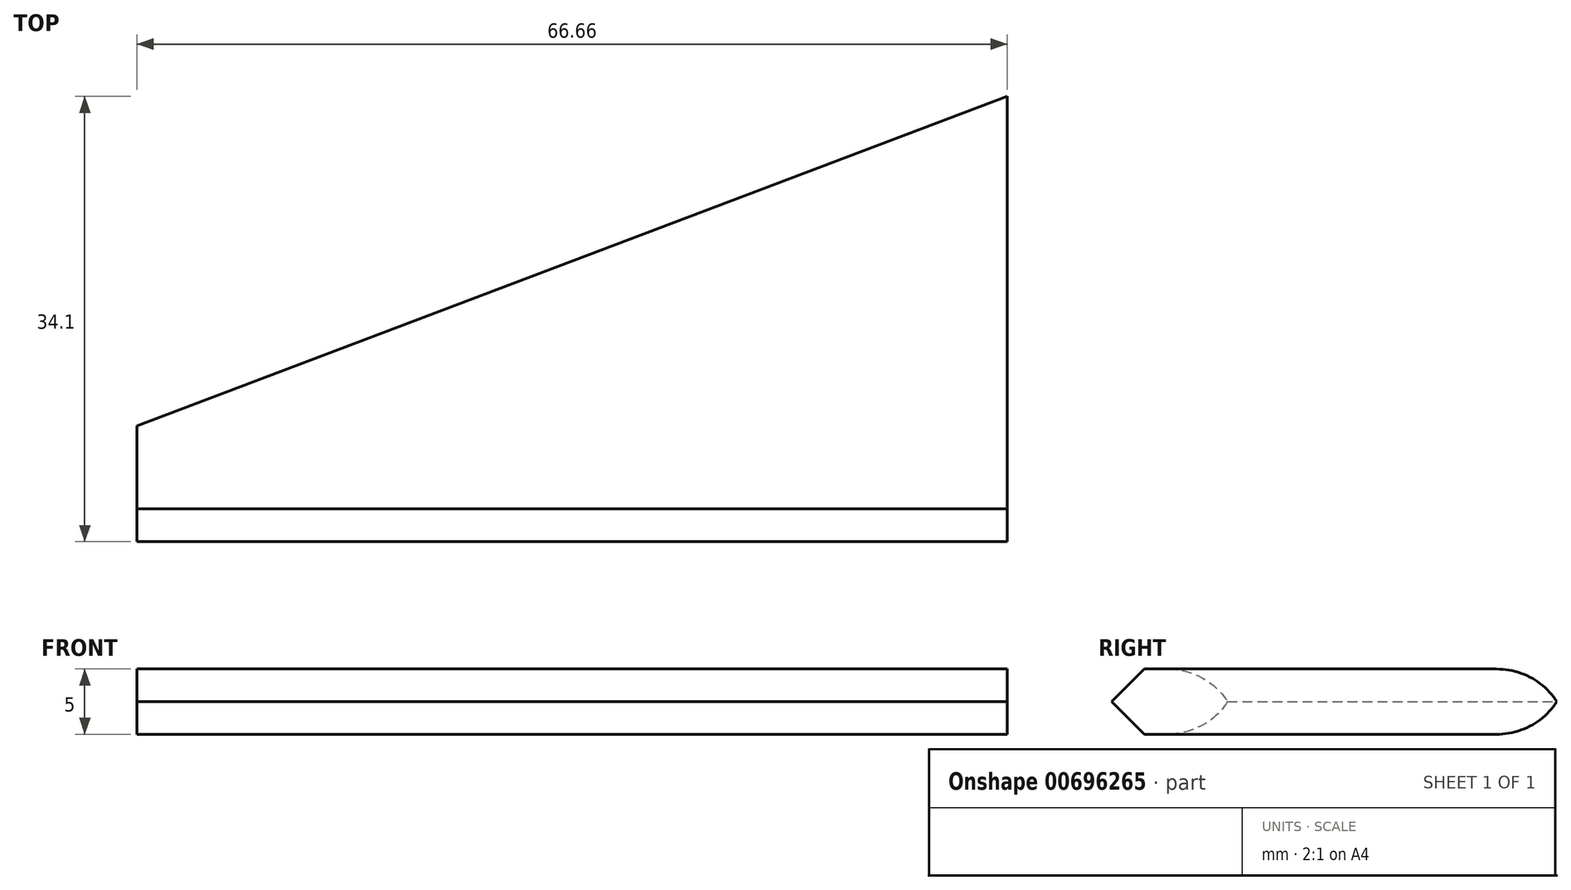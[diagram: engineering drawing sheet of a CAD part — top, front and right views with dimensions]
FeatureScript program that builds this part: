
annotation { "Feature Type Name" : "Feature", "Feature Type Description" : "" }
export const myFeature = defineFeature(function(context is Context, id is Id, definition is map)
    precondition{}
    {
        {
            var Q0;
            Q0=qCreatedBy(makeId("Top.planeOp"),FACE);
            var sketch = newSketch(context, id + "F0", { "sketchPlane" : qUnion([Q0])});
            skLineSegment(sketch, "E0.bottom", {"start": v(33.33, -6.05) * mm, "end": v(-33.33, -6.05) * mm});
            skLineSegment(sketch, "E0.top", {"start": v(33.33, 6.05) * mm, "end": v(-33.33, 6.05) * mm});
            skLineSegment(sketch, "E0.left", {"start": v(33.33, -6.05) * mm, "end": v(33.33, 6.05) * mm});
            skLineSegment(sketch, "E0.right", {"start": v(-33.33, -6.05) * mm, "end": v(-33.33, 6.05) * mm});
            skPoint(sketch, "E0.middle", {"position": v(0, 0) * mm});
            skLineSegment(sketch, "E1", {"start": v(-33.33, 6.05) * mm, "end": v(33.33, 31.27) * mm});
            skLineSegment(sketch, "E2", {"start": v(33.33, 31.27) * mm, "end": v(33.33, 6.05) * mm});
            skSolve(sketch);
        }
        {
            var Q0;
            Q0=makeQuery(id+"F0.imprint","IMPRINT",FACE,{"disambiguationData":[TD([[makeQuery(id+"F0.imprint","IMPRINT",EDGE,{"derivedFrom":sQuery(id+"F0.wireOp",EDGE,"E0.top")}),-1.0]])]});
            var Q1;
            Q1=makeQuery(id+"F0.imprint","IMPRINT",FACE,{"disambiguationData":[TD([[makeQuery(id+"F0.imprint","IMPRINT",EDGE,{"derivedFrom":sQuery(id+"F0.wireOp",EDGE,"E0.bottom")}),-1.0]])]});
            extrude(context, id + "F1", {"entities" : qUnion([Q0, Q1]), "depth" : 5 * mm, "offsetDistance" : 25 * mm});
        }
        {
            var Q0;
            Q0=makeQuery(id+"F1.opExtrude","CAP_EDGE",EDGE,{"disambiguationData":[OSD([sQuery(id+"F0.wireOp",EDGE,"E1")])],"isStart":false});
            var Q1;
            Q1=makeQuery(id+"F1.opExtrude","CAP_EDGE",EDGE,{"disambiguationData":[OSD([sQuery(id+"F0.wireOp",EDGE,"E1")])],"isStart":true});
            fillet(context, id + "F2", {"entities" : qUnion([Q0, Q1]), "radius" : 5 * mm, "tangentPropagation" : true, "allowEdgeOverflow" : false});
        }
        {
            var Q0;
            Q0=makeQuery(id+"F1.opExtrude","CAP_EDGE",EDGE,{"disambiguationData":[OSD([sQuery(id+"F0.wireOp",EDGE,"E0.bottom")])],"isStart":false});
            var Q1;
            Q1=makeQuery(id+"F1.opExtrude","CAP_EDGE",EDGE,{"disambiguationData":[OSD([sQuery(id+"F0.wireOp",EDGE,"E0.bottom")])],"isStart":true});
            chamfer(context, id + "F3", {"entities" : qUnion([Q0, Q1]), "width" : 5 * mm, "tangentPropagation" : true});
        }
    });
